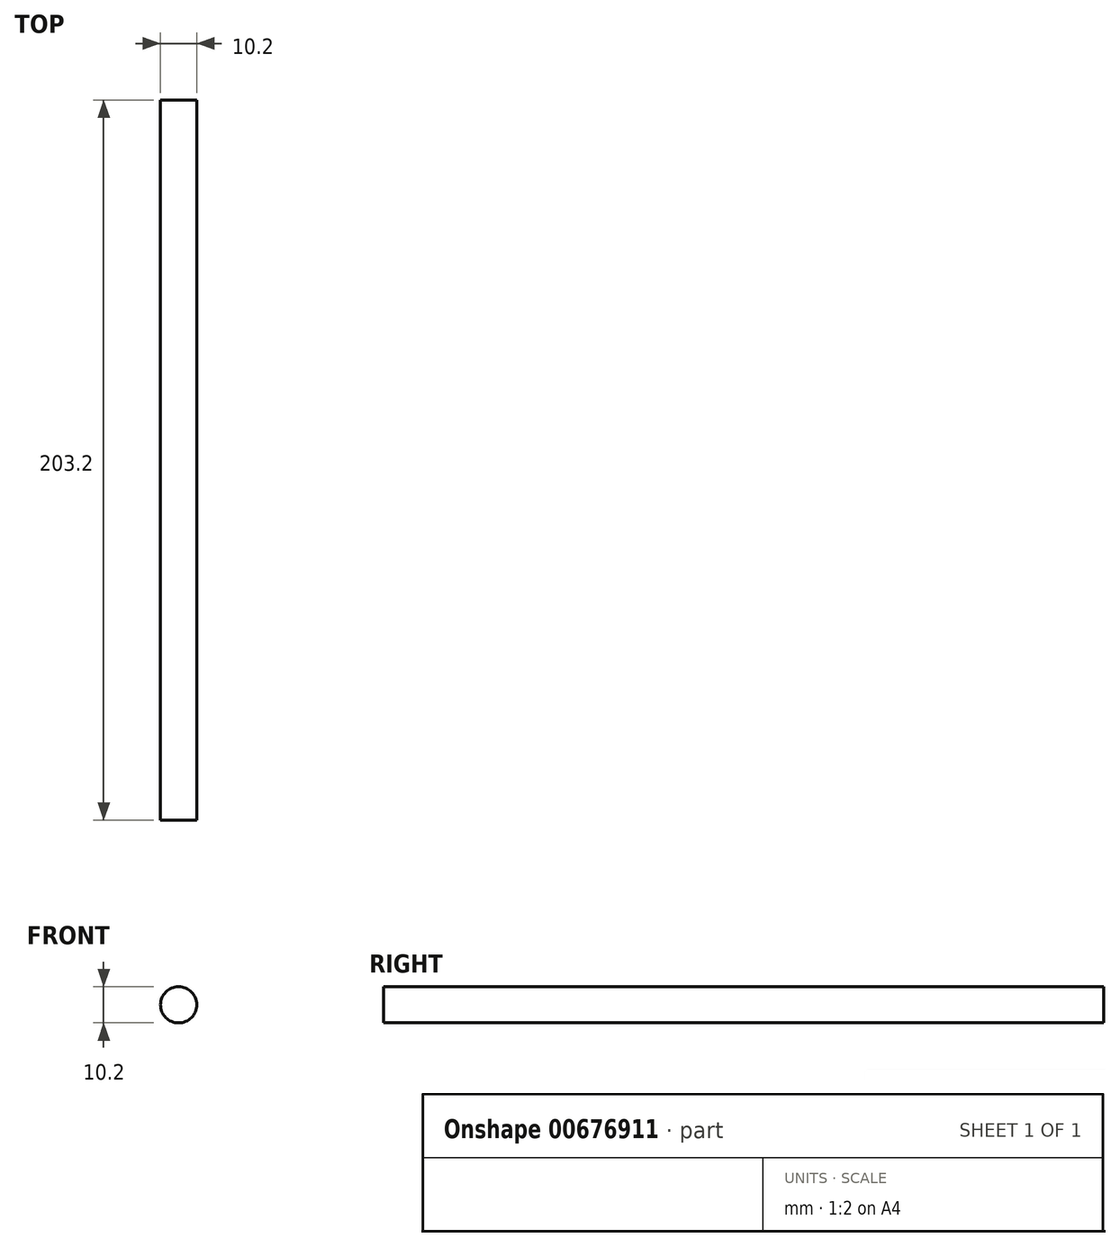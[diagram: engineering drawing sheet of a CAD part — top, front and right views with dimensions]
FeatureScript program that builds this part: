
annotation { "Feature Type Name" : "Feature", "Feature Type Description" : "" }
export const myFeature = defineFeature(function(context is Context, id is Id, definition is map)
    precondition{}
    {
        {
            var Q0;
            Q0=qCreatedBy(makeId("Front.planeOp"),FACE);
            var sketch = newSketch(context, id + "F0", { "sketchPlane" : qUnion([Q0])});
            skCircle(sketch, "E0", {"center": v(0, 0) * mm, "radius": 5.1 * mm});
            skSolve(sketch);
        }
        {
            var Q0;
            Q0=makeQuery(id+"F0.imprint","IMPRINT",FACE,{"disambiguationData":[TD([[makeQuery(id+"F0.imprint","IMPRINT",EDGE,{"derivedFrom":sQuery(id+"F0.wireOp",EDGE,"E0")}),1.0]])]});
            var Q1;
            Q1=sQuery(id+"F0.wireOp",EDGE,"E0");
            extrude(context, id + "F1", {"entities" : qUnion([Q0]), "surfaceEntities" : qUnion([Q1]), "depth" : 101.6 * mm, "offsetDistance" : 25.4 * mm, "hasSecondDirection" : true, "secondDirectionOppositeDirection" : true, "secondDirectionDepth" : 101.6 * mm});
        }
    });
